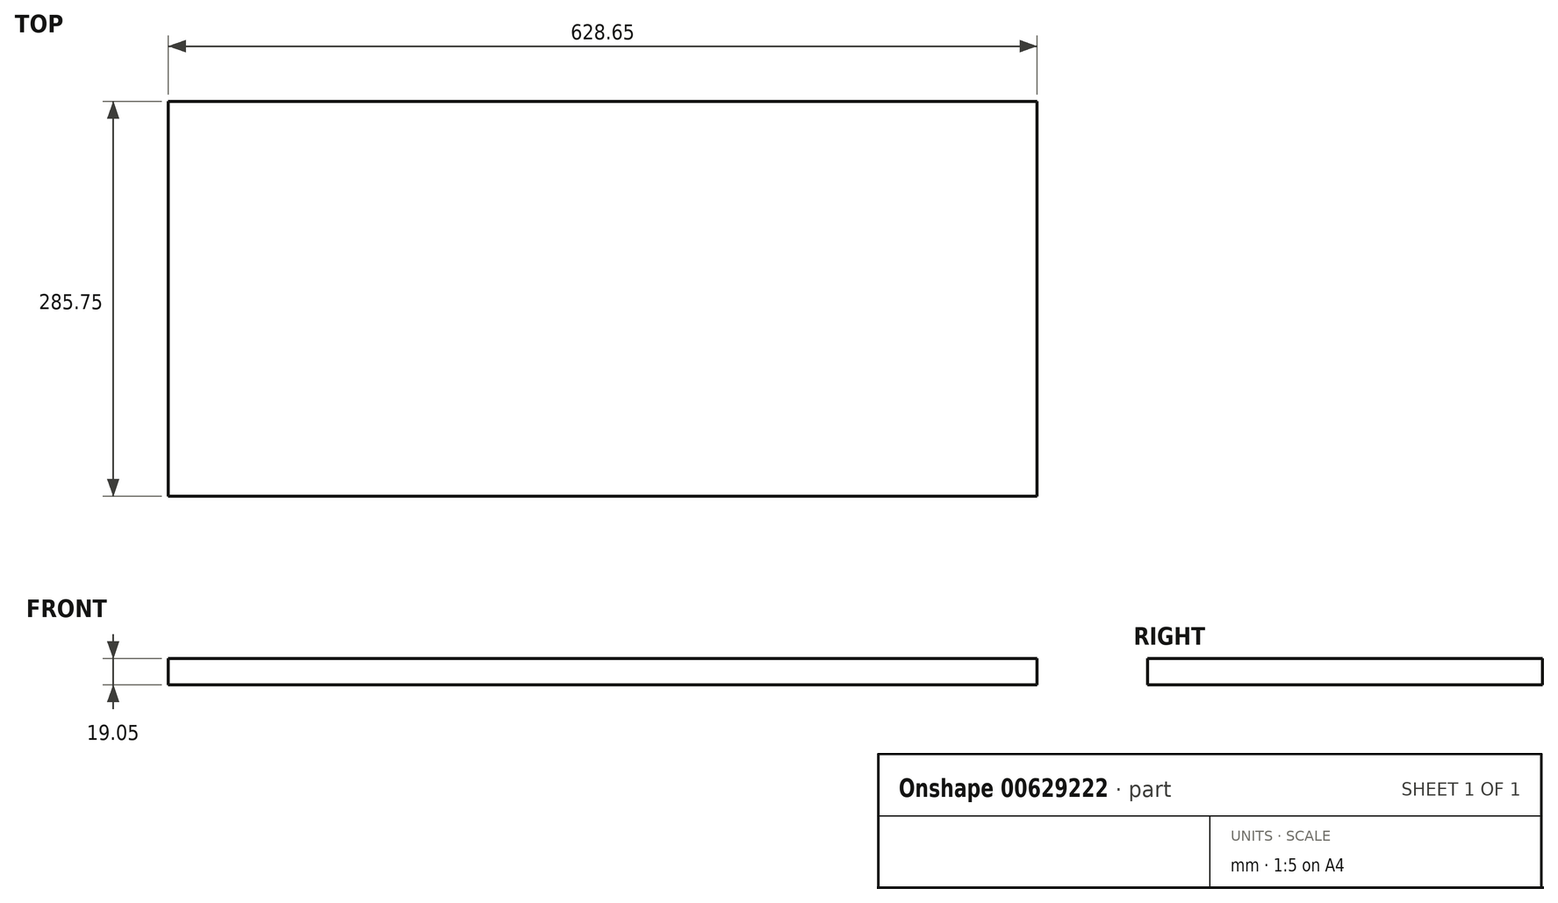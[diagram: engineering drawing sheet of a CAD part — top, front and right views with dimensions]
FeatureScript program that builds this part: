
annotation { "Feature Type Name" : "Feature", "Feature Type Description" : "" }
export const myFeature = defineFeature(function(context is Context, id is Id, definition is map)
    precondition{}
    {
        {
            var Q0;
            Q0=qCreatedBy(makeId("Top.planeOp"),FACE);
            var sketch = newSketch(context, id + "F0", { "sketchPlane" : qUnion([Q0])});
            skLineSegment(sketch, "E0.bottom", {"start": v(0, 0) * mm, "end": v(-628.65, 0) * mm});
            skLineSegment(sketch, "E0.top", {"start": v(0, -285.75) * mm, "end": v(-628.65, -285.75) * mm});
            skLineSegment(sketch, "E0.left", {"start": v(0, 0) * mm, "end": v(0, -285.75) * mm});
            skLineSegment(sketch, "E0.right", {"start": v(-628.65, 0) * mm, "end": v(-628.65, -285.75) * mm});
            skLineSegment(sketch, "E1", {"start": v(-612.78, -285.75) * mm, "end": v(-612.78, 0) * mm});
            skLineSegment(sketch, "E2", {"start": v(-15.88, 0) * mm, "end": v(-15.87, -285.75) * mm});
            skLineSegment(sketch, "E3", {"start": v(-628.65, -269.88) * mm, "end": v(0, -269.88) * mm});
            skLineSegment(sketch, "E4", {"start": v(-628.65, -15.88) * mm, "end": v(0, -15.87) * mm});
            skSolve(sketch);
        }
        {
            var Q0;
            {var subQ0=sQuery(id+"F0.wireOp",EDGE,"E3");var subQ1=sQuery(id+"F0.wireOp",EDGE,"E1");var subQ2=makeQuery(id+"F0.imprint","INTERSECT",VERTEX,{"derivedFrom":[subQ1,subQ0]});Q0=makeQuery(id+"F0.imprint","IMPRINT",FACE,{"disambiguationData":[TD([[makeQuery(id+"F0.imprint","IMPRINT",EDGE,{"disambiguationData":[TD([[subQ2,-1.0]])],"derivedFrom":subQ1}),-1.0]])]});}
            var Q1;
            {var subQ0=sQuery(id+"F0.wireOp",EDGE,"E1");var subQ1=sQuery(id+"F0.wireOp",EDGE,"E0.bottom");var subQ2=makeQuery(id+"F0.imprint","INTERSECT",VERTEX,{"derivedFrom":[subQ1,subQ0]});Q1=makeQuery(id+"F0.imprint","IMPRINT",FACE,{"disambiguationData":[TD([[makeQuery(id+"F0.imprint","IMPRINT",EDGE,{"disambiguationData":[TD([[subQ2,1.0]])],"derivedFrom":subQ1}),1.0]])]});}
            var Q2;
            {var subQ0=sQuery(id+"F0.wireOp",EDGE,"E3");var subQ1=sQuery(id+"F0.wireOp",EDGE,"E0.right");var subQ2=makeQuery(id+"F0.imprint","INTERSECT",VERTEX,{"derivedFrom":[subQ1,subQ0]});Q2=makeQuery(id+"F0.imprint","IMPRINT",FACE,{"disambiguationData":[TD([[makeQuery(id+"F0.imprint","IMPRINT",EDGE,{"disambiguationData":[TD([[subQ2,1.0]])],"derivedFrom":subQ1}),1.0]])]});}
            var Q3;
            {var subQ0=sQuery(id+"F0.wireOp",EDGE,"E1");var subQ1=sQuery(id+"F0.wireOp",EDGE,"E0.top");var subQ2=makeQuery(id+"F0.imprint","INTERSECT",VERTEX,{"derivedFrom":[subQ1,subQ0]});Q3=makeQuery(id+"F0.imprint","IMPRINT",FACE,{"disambiguationData":[TD([[makeQuery(id+"F0.imprint","IMPRINT",EDGE,{"disambiguationData":[TD([[subQ2,1.0]])],"derivedFrom":subQ1}),-1.0]])]});}
            var Q4;
            {var subQ0=sQuery(id+"F0.wireOp",EDGE,"E3");var subQ1=sQuery(id+"F0.wireOp",EDGE,"E0.left");var subQ2=makeQuery(id+"F0.imprint","INTERSECT",VERTEX,{"derivedFrom":[subQ1,subQ0]});Q4=makeQuery(id+"F0.imprint","IMPRINT",FACE,{"disambiguationData":[TD([[makeQuery(id+"F0.imprint","IMPRINT",EDGE,{"disambiguationData":[TD([[subQ2,1.0]])],"derivedFrom":subQ1}),-1.0]])]});}
            var Q5;
            {var subQ0=sQuery(id+"F0.wireOp",EDGE,"E0.right");var subQ1=sQuery(id+"F0.wireOp",EDGE,"E0.top");var subQ2=makeQuery(id+"F0.imprint","INTERSECT",VERTEX,{"derivedFrom":[subQ1,subQ0]});Q5=makeQuery(id+"F0.imprint","IMPRINT",FACE,{"disambiguationData":[TD([[makeQuery(id+"F0.imprint","IMPRINT",EDGE,{"disambiguationData":[TD([[subQ2,1.0]])],"derivedFrom":subQ1}),-1.0]])]});}
            var Q6;
            {var subQ0=sQuery(id+"F0.wireOp",EDGE,"E0.left");var subQ1=sQuery(id+"F0.wireOp",EDGE,"E0.top");var subQ2=makeQuery(id+"F0.imprint","INTERSECT",VERTEX,{"derivedFrom":[subQ1,subQ0]});Q6=makeQuery(id+"F0.imprint","IMPRINT",FACE,{"disambiguationData":[TD([[makeQuery(id+"F0.imprint","IMPRINT",EDGE,{"disambiguationData":[TD([[subQ2,-1.0]])],"derivedFrom":subQ1}),-1.0]])]});}
            var Q7;
            {var subQ0=sQuery(id+"F0.wireOp",EDGE,"E0.left");var subQ1=sQuery(id+"F0.wireOp",EDGE,"E0.bottom");var subQ2=makeQuery(id+"F0.imprint","INTERSECT",VERTEX,{"derivedFrom":[subQ1,subQ0]});Q7=makeQuery(id+"F0.imprint","IMPRINT",FACE,{"disambiguationData":[TD([[makeQuery(id+"F0.imprint","IMPRINT",EDGE,{"disambiguationData":[TD([[subQ2,-1.0]])],"derivedFrom":subQ1}),1.0]])]});}
            var Q8;
            {var subQ0=sQuery(id+"F0.wireOp",EDGE,"E0.right");var subQ1=sQuery(id+"F0.wireOp",EDGE,"E0.bottom");var subQ2=makeQuery(id+"F0.imprint","INTERSECT",VERTEX,{"derivedFrom":[subQ1,subQ0]});Q8=makeQuery(id+"F0.imprint","IMPRINT",FACE,{"disambiguationData":[TD([[makeQuery(id+"F0.imprint","IMPRINT",EDGE,{"disambiguationData":[TD([[subQ2,1.0]])],"derivedFrom":subQ1}),1.0]])]});}
            extrude(context, id + "F1", {"entities" : qUnion([Q0, Q1, Q2, Q3, Q4, Q5, Q6, Q7, Q8]), "depth" : 19.05 * mm, "offsetDistance" : 25.4 * mm});
        }
    });
